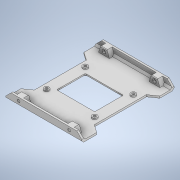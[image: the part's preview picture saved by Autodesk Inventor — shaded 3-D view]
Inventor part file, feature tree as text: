
AUTODESK INVENTOR PART (.ipt)
format: ipt  version: 2022 (Build 260153000, 153)  size: 353,792 bytes
history: native  units: in
note: dims shown in document units (in); Inventor stores cm internally (conversion verified against a paired STEP export)
features: extrude x9, sketch x9, projected_geometry x6, chamfer x3, fillet x3, draft x2, plane x2, mirror x2, pattern_linear x1
ambient origin geometry x8: Origin, YZ Plane, XZ Plane, XY Plane, X Axis, Y Axis, Z Axis, Center Point
bodies: Solid1 (feature_tree)
feature tree (37):
  extrude  "Extrusion1"  Depth=5.748in
  extrude  "Extrusion2"  Depth=0.1181in
  chamfer  "Chamfer1"  Distance=0.3937in
  extrude  "Extrusion6"  Depth=1.5748in
  extrude  "Extrusion7"  Depth=0.3937in TaperAngle=0.0deg
  extrude  "Extrusion9"  Depth=2.4154in
  extrude  "Extrusion10"  Depth=0.1575in
  chamfer  "Chamfer2"  [1 undecoded]
  draft  "FaceDraft2"
  draft  "FaceDraft3"
  extrude  "Extrusion12"  Depth=0.0787in
  fillet  "Fillet3"  Radius=0.9963in
  pattern_linear  "Rectangular Pattern3"  Spacing1=0.9963in  [1 undecoded]
  plane  "Work Plane3"
  mirror  "Mirror2"
  extrude  "Extrusion13"  TaperAngle=0.0deg  [1 undecoded]
  plane  "Work Plane5"
  mirror  "Mirror4"
  fillet  "Fillet4"  Radius=0.1969in
  fillet  "Fillet5"  Radius=0.1969in
  chamfer  "Chamfer3"  Distance=0.315in
  extrude  "Extrusion14"  Depth=0.315in TaperAngle=45.0deg
  sketch  "Sketch1"  dims[d0=4.7244in d1=5.748in]
  sketch  "Sketch2"  dims[d2=0.1181in d3=0.0in d4=0.1181in d5=0.3937in d6=0.0in]
  projected_geometry  "Projected Loop1"
  sketch  "Sketch6"  dims[d17=0.1181in d18=0.0787in d19=45.0deg d31=1.5748in]
  projected_geometry  "Projected Loop5"
  sketch  "Sketch8"  dims[d33=0.1378in d34=0.3937in d35=0.0in]
  projected_geometry  "Projected Loop7"
  sketch  "Sketch10"  dims[d36=2.998in d37=2.4154in]
  projected_geometry  "Projected Loop10"
  sketch  "Sketch13"  dims[d38=0.1575in d39=0.1575in]
  projected_geometry  "Projected Loop11"
  projected_geometry  "Projected Loop12"
  sketch  "Sketch16"  dims[d40=0.1575in]
  sketch  "Sketch17"  dims[d41=0.1575in d42=0.0in d43=0.0in]
  sketch  "Sketch19"  dims[d55=0.9843in d56=3.937in d57=0.9963in d58=0.9963in d59=0.0in d60=0.0in d61=0.1969in d62=0.1969in d63=0.315in d64=0.0in d70=0.315in d71=0.0787in d72=45.0deg d73=0.1374in d74=0.1374in d75=0.2165in d76=0.1181in d77=0.0in d78=0.0394in d79=0.7874in d81=3.1496in d82=0.315in d83=0.0in d84=0.0in d85=0.0197in d87=0.0787in d88=0.0394in d89=0.0787in d90=45.0deg d91=0.0787in d92=0.0787in d93=0.0787in d94=0.0787in d95=0.0787in d96=0.0in]
note: 3 required parameter values undecoded (feature->parameter linkage not recoverable at this tier; creation-order binding heuristic only, values carry confidence <= 0.55)
